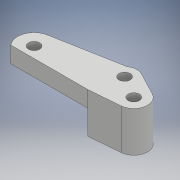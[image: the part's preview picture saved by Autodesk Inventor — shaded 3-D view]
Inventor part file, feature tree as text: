
AUTODESK INVENTOR PART (.ipt)
format: ipt  version: 2017 (Build 210142000, 142)  size: 449,024 bytes
history: native  units: mm
features: extrude x40, sketch x40, shell x1
ambient origin geometry x8: Origin, YZ Plane, XZ Plane, XY Plane, X Axis, Y Axis, Z Axis, Center Point
bodies: Solid1 (feature_tree)
feature tree (81):
  extrude  "Extrusion1"  Depth=37.0mm
  shell  "Shell1"  Thickness=20.0mm
  extrude  "Extrusion2"  Depth=55.0mm
  extrude  "Extrusion3"  TaperAngle=0.0deg  [1 undecoded]
  extrude  "Extrusion4"  Depth=5.0mm
  extrude  "Extrusion5"  TaperAngle=0.0deg  [1 undecoded]
  extrude  "Extrusion6"  Depth=10.0mm TaperAngle=0.0deg
  extrude  "Extrusion7"  Depth=15.0mm TaperAngle=0.0deg
  extrude  "Extrusion9"  Depth=8.5mm
  extrude  "Extrusion10"  Depth=15.0mm TaperAngle=0.0deg
  extrude  "Extrusion11"  Depth=35.46mm
  extrude  "Extrusion12"  Depth=15.0mm TaperAngle=0.0deg
  extrude  "Extrusion13"  Depth=4.5mm
  extrude  "Extrusion14"  Depth=15.0mm TaperAngle=0.0deg
  extrude  "Extrusion15"  Depth=8.5mm
  extrude  "Extrusion16"  Depth=15.0mm TaperAngle=0.0deg
  extrude  "Extrusion17"  Depth=28.505mm
  extrude  "Extrusion18"  Depth=15.0mm TaperAngle=0.0deg
  extrude  "Extrusion19"  Depth=36.0mm
  extrude  "Extrusion20"  Depth=15.0mm TaperAngle=0.0deg
  extrude  "Extrusion23"  Depth=50.0mm
  extrude  "Extrusion21"  Depth=4.1656mm
  extrude  "Extrusion22"  Depth=35.46mm
  extrude  "Extrusion24"  Depth=10.0mm
  extrude  "Extrusion25"  Depth=10.0mm TaperAngle=0.0deg
  extrude  "Extrusion26"  Depth=2.583mm TaperAngle=0.0deg
  extrude  "Extrusion27"  Depth=2.583mm TaperAngle=0.0deg
  extrude  "Extrusion28"  Depth=100.0mm TaperAngle=0.0deg
  extrude  "Extrusion29"  Depth=5.0mm
  extrude  "Extrusion30"  Depth=1.0mm
  extrude  "Extrusion31"  Depth=5.0mm
  extrude  "Extrusion32"  Depth=4.1656mm
  extrude  "Extrusion33"  Depth=6.161mm
  extrude  "Extrusion34"  Depth=4.1656mm
  extrude  "Extrusion35"  Depth=15.906mm
  extrude  "Extrusion36"  Depth=22.5mm TaperAngle=0.0deg
  extrude  "Extrusion37"  Depth=22.5mm TaperAngle=0.0deg
  extrude  "Extrusion38"  Depth=9.0mm
  extrude  "Extrusion39"  TaperAngle=0.0deg  [1 undecoded]
  extrude  "Extrusion40"  Depth=4.1656mm
  extrude  "Extrusion41"  Depth=15.0mm
  sketch  "Sketch1"  dims[d0=35.0mm d1=37.0mm d2=20.0mm]
  sketch  "Sketch2"  dims[d3=11.0mm d4=55.0mm]
  sketch  "Sketch3"  dims[d5=26.0mm d6=0.0mm]
  sketch  "Sketch4"  dims[d7=50.0mm d8=0.0mm d9=5.0mm]
  sketch  "Sketch5"  dims[d10=17.0mm d11=0.0mm]
  sketch  "Sketch6"  dims[d12=11.0mm d13=10.0mm d14=0.0mm]
  sketch  "Sketch7"  dims[d15=15.0mm d16=0.0mm d17=15.0mm d18=0.0mm]
  sketch  "Sketch13"  dims[d19=4.1656mm d20=8.5mm]
  sketch  "Sketch14"  dims[d21=11.5mm d22=15.0mm d23=0.0mm]
  sketch  "Sketch15"  dims[d24=4.1656mm d25=35.46mm]
  sketch  "Sketch16"  dims[d26=23.505mm d27=15.0mm d28=0.0mm]
  sketch  "Sketch17"  dims[d29=4.1656mm d30=4.5mm]
  sketch  "Sketch18"  dims[d31=14.0mm d32=15.0mm d33=0.0mm]
  sketch  "Sketch20"  dims[d41=4.1656mm d42=8.5mm]
  sketch  "Sketch21"  dims[d43=11.5mm d44=15.0mm d45=0.0mm]
  sketch  "Sketch22"  dims[d46=4.1656mm d47=28.505mm]
  sketch  "Sketch23"  dims[d48=35.46mm d49=15.0mm d50=0.0mm]
  sketch  "Sketch24"  dims[d51=4.1656mm d52=36.0mm]
  sketch  "Sketch25"  dims[d53=4.5mm d54=15.0mm d55=0.0mm]
  sketch  "Sketch26"  dims[d56=5.0mm d57=50.0mm]
  sketch  "Sketch27"  dims[d58=21.0mm d59=0.0mm d60=4.1656mm]
  sketch  "Sketch28"  dims[d61=23.505mm d62=35.46mm]
  sketch  "Sketch29"  dims[d63=10.0mm d64=0.0mm d65=4.1656mm]
  sketch  "Sketch30"  dims[d67=36.0mm d68=10.0mm d69=0.0mm]
  sketch  "Sketch31"  dims[d70=4.5mm d71=2.583mm d72=0.0mm]
  sketch  "Sketch33"  dims[d73=2.583mm d74=0.0mm d75=2.583mm d76=0.0mm]
  sketch  "Sketch34"  dims[d77=6.917mm d78=100.0mm d79=0.0mm]
  sketch  "Sketch35"  dims[d80=5.0mm d81=5.0mm]
  sketch  "Sketch39"  dims[d83=1.0mm d84=1.0mm]
  sketch  "Sketch40"  dims[d85=100.0mm d86=0.0mm d87=5.0mm]
  sketch  "Sketch41"  dims[d88=22.5mm d89=0.0mm d90=4.1656mm]
  sketch  "Sketch42"  dims[d91=5.851mm d92=6.161mm]
  sketch  "Sketch43"  dims[d93=25.0mm d94=0.0mm d95=4.1656mm]
  sketch  "Sketch44"  dims[d96=2.702mm d97=15.906mm]
  sketch  "Sketch45"  dims[d98=25.0mm d99=0.0mm d100=22.5mm d101=0.0mm]
  sketch  "Sketch47"  dims[d102=2.5mm d103=22.5mm d104=0.0mm]
  sketch  "Sketch48"  dims[d105=9.0mm d106=5.0mm]
  sketch  "Sketch49"  dims[d107=5.0mm d108=0.0mm]
  sketch  "Sketch50"  dims[d109=30.0mm d110=0.0mm d111=4.1656mm]
  sketch  "Sketch51"  dims[d112=6.083mm d113=4.0mm d114=30.0mm d115=0.0mm d116=30.0mm d117=0.0mm d118=30.0mm d119=0.0mm d120=8.0mm d121=0.0mm d130=11.0mm d131=15.0mm d132=0.0mm d133=0.0mm d134=5.0mm d135=0.0mm d136=190.0mm d137=0.0mm d138=50.0mm d139=0.0mm d140=50.0mm d141=0.0mm d142=15.0mm d143=0.0mm d144=3.0mm d145=3.0mm d146=5.0mm d147=1.0mm d148=1.0mm d149=5.0mm d150=0.0mm d151=3.0mm d152=1.0mm d153=3.0mm d154=1.0mm d155=5.0mm d156=5.0mm d157=0.0mm d158=135.0deg d159=4.1656mm d160=15.0mm d161=0.0mm d162=3.0mm d163=15.0mm d164=0.0mm d165=4.1656mm d166=0.0mm d167=0.0mm d168=15.0mm d169=0.0mm d170=15.0mm d171=0.0mm d172=15.0mm d173=0.0mm d174=5.0mm d175=0.0mm]
note: 3 required parameter values undecoded (feature->parameter linkage not recoverable at this tier; creation-order binding heuristic only, values carry confidence <= 0.55)
